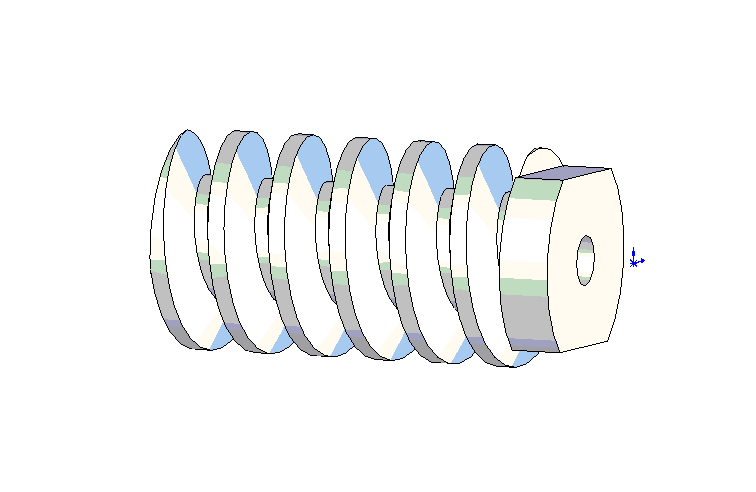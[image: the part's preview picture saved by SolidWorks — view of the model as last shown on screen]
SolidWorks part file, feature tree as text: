
SOLIDWORKS PART (.sldprt)
format: sldprt  version: not decoded by parser v0  size: 263,680 bytes
history: native  units: mm
features: sketch x6, plane x3, extrude x3, material x1, helix x1, sweep x1, cut_extrude x1 (+10 scaffold rows collapsed)
feature tree (26):
  scaffold x10  (default folders/planes/origin — collapsed)
  material  "Matériau <non spécifié>"
  plane  "Plan de face"
  plane  "Plan de dessus"
  plane  "Plan de droite"
  sketch  "Esquisse1"  dims[D1=2.533mm D2=~1.00133mm]
  extrude  "Extrusion1"  Depth=10mm
  sketch  "Esquisse3"
  helix  "Hélice/Spirale1"  Pitch=10.750545mm
  sketch  "Esquisse4"  dims[c1.D1=~0.730448mm c2.D1=70.0deg c2.D2=~0.730448mm c3.D2=70.0deg c3.D3=2.167mm c3.D4=0.17mm c3.D5=0.17mm]
  sweep  "Balayage1"
  sketch  "Esquisse5"  dims[D1=7.3mm D2=2.0mm]
  cut_extrude  "Enlèv. mat.-Extru.1"  Depth=20mm
  sketch  "Esquisse7"  dims[D1=4.333mm D2=1.7mm D3=1.7mm]
  extrude  "Extrusion2"  Depth=1mm
  sketch  "Esquisse8"  dims[D1=1.0mm]
  extrude  "Enlèv. mat.-Extru.2"  Depth=30mm
decode coverage: 10 of 12 modeling features carry decoded parameters
note: ~ marks probable driven/reference dimensions
note: suppression state not decoded; provenance and decode notes live in map.json
